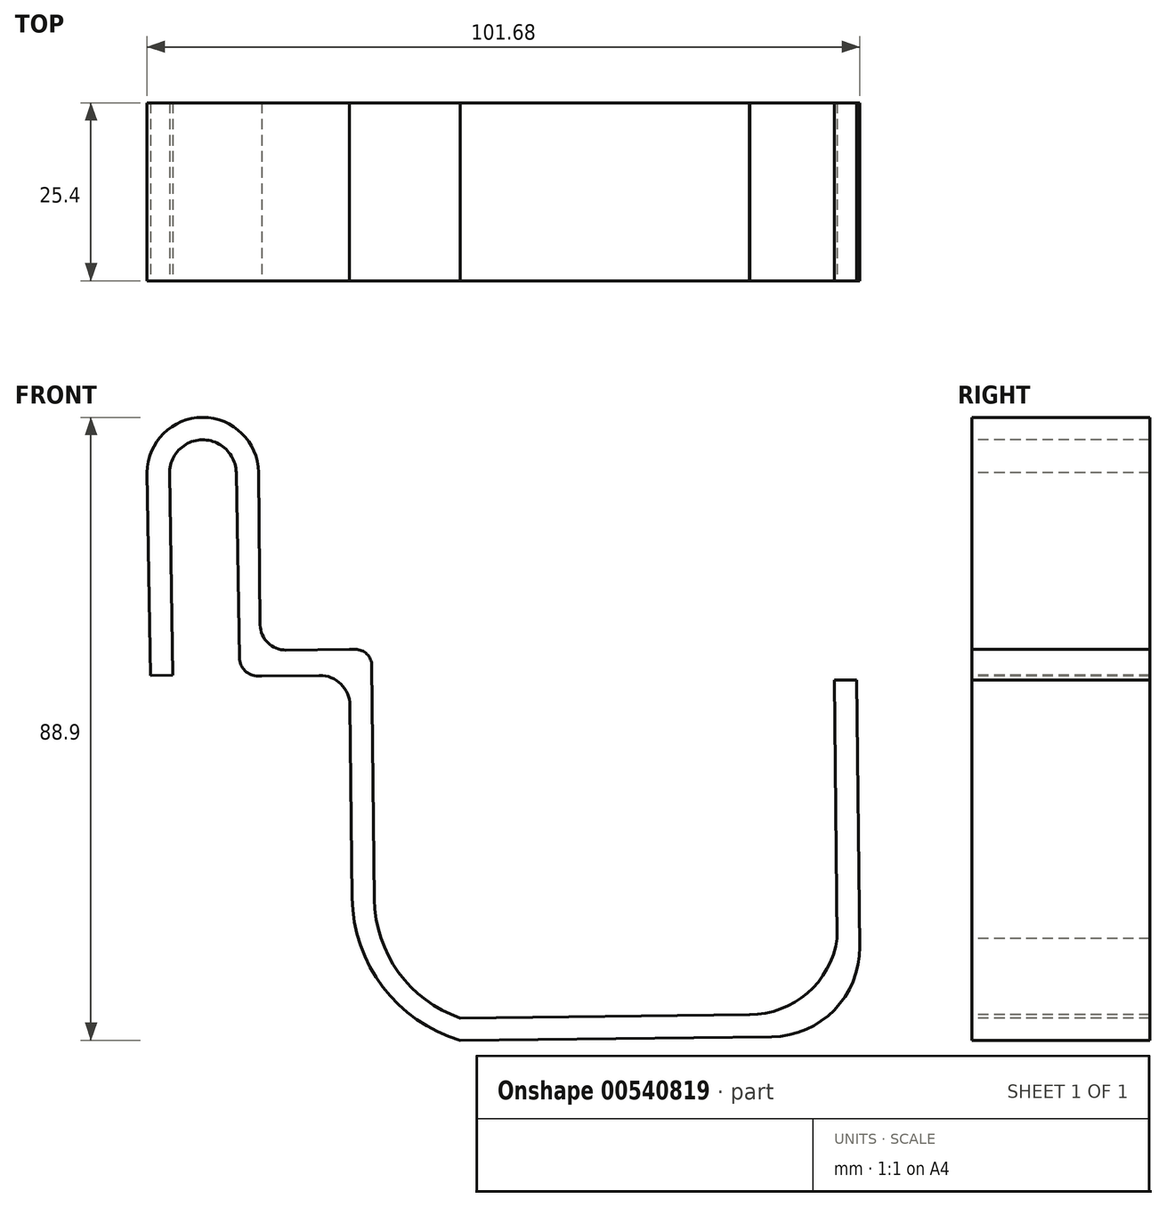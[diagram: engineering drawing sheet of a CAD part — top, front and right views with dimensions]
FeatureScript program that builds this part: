
annotation { "Feature Type Name" : "Feature", "Feature Type Description" : "" }
export const myFeature = defineFeature(function(context is Context, id is Id, definition is map)
    precondition{}
    {
        {
            var Q0;
            Q0=qCreatedBy(makeId("Front.planeOp"),FACE);
            var sketch = newSketch(context, id + "F0", { "sketchPlane" : qUnion([Q0])});
            skLineSegment(sketch, "E0", {"start": v(-53.92, 53.44) * mm, "end": v(-53.55, 20.1) * mm});
            skArc(sketch, "E1", {"start": v(-53.55, 20.1) * mm, "mid": v(-50.12, 9.7) * mm, "end": v(-41.31, 3.17) * mm});
            skLineSegment(sketch, "E2", {"start": v(-41.31, 3.17) * mm, "end": v(0, 3.64) * mm});
            skLineSegment(sketch, "E3", {"start": v(-41.31, 0) * mm, "end": v(3.14, 0.5) * mm});
            skLineSegment(sketch, "E4", {"start": v(-57.04, 47.78) * mm, "end": v(-56.73, 20.32) * mm});
            skLineSegment(sketch, "E5", {"start": v(15.7, 13.34) * mm, "end": v(15.27, 51.44) * mm});
            skLineSegment(sketch, "E6", {"start": v(15.27, 51.44) * mm, "end": v(12.1, 51.4) * mm});
            skLineSegment(sketch, "E7", {"start": v(12.1, 51.4) * mm, "end": v(12.5, 14.5) * mm});
            skLineSegment(sketch, "E8", {"start": v(-0.06, 3.64) * mm, "end": v(0, 3.64) * mm});
            skArc(sketch, "E9.filletArc", {"start": v(-0.06, 3.64) * mm, "mid": v(8.24, 6.73) * mm, "end": v(12.5, 14.5) * mm});
            skArc(sketch, "E10.filletArc", {"start": v(3.14, 0.5) * mm, "mid": v(12.07, 4.32) * mm, "end": v(15.7, 13.34) * mm});
            skArc(sketch, "E11", {"start": v(-56.73, 20.32) * mm, "mid": v(-52.38, 7.62) * mm, "end": v(-41.31, 0) * mm});
            skLineSegment(sketch, "E12", {"start": v(-57.13, 55.79) * mm, "end": v(-66.17, 55.69) * mm});
            skLineSegment(sketch, "E13", {"start": v(-57.13, 55.79) * mm, "end": v(-56.3, 55.79) * mm});
            skLineSegment(sketch, "E14", {"start": v(-61.42, 52.07) * mm, "end": v(-69.6, 51.98) * mm});
            skLineSegment(sketch, "E15", {"start": v(-69.87, 59.3) * mm, "end": v(-70.1, 81.05) * mm});
            skLineSegment(sketch, "E16", {"start": v(-69.6, 51.98) * mm, "end": v(-70.15, 51.98) * mm});
            skLineSegment(sketch, "E17", {"start": v(-72.83, 54.6) * mm, "end": v(-73.28, 81.01) * mm});
            skLineSegment(sketch, "E18", {"start": v(-82.8, 80.84) * mm, "end": v(-82.3, 52.12) * mm});
            skLineSegment(sketch, "E19", {"start": v(-82.3, 52.12) * mm, "end": v(-85.48, 52.07) * mm});
            skLineSegment(sketch, "E20", {"start": v(-85.48, 52.07) * mm, "end": v(-85.99, 81.01) * mm});
            skArc(sketch, "E21", {"start": v(-70.1, 81.05) * mm, "mid": v(-78.06, 88.9) * mm, "end": v(-85.99, 81.01) * mm});
            skArc(sketch, "E22", {"start": v(-73.28, 81.01) * mm, "mid": v(-78.13, 85.69) * mm, "end": v(-82.8, 80.84) * mm});
            skArc(sketch, "E23.filletArc", {"start": v(-57.04, 47.78) * mm, "mid": v(-58.34, 50.83) * mm, "end": v(-61.42, 52.07) * mm});
            skArc(sketch, "E24.filletArc", {"start": v(-53.92, 53.44) * mm, "mid": v(-54.63, 55.1) * mm, "end": v(-56.3, 55.79) * mm});
            skArc(sketch, "E25.filletArc", {"start": v(-69.87, 59.3) * mm, "mid": v(-68.77, 56.73) * mm, "end": v(-66.17, 55.69) * mm});
            skArc(sketch, "E26.filletArc", {"start": v(-72.83, 54.6) * mm, "mid": v(-72.03, 52.75) * mm, "end": v(-70.15, 51.98) * mm});
            skSolve(sketch);
        }
        {
            var Q0;
            Q0=sQuery(id+"F0.wireOp",EDGE,"E18");
            var Q1;
            Q1=sQuery(id+"F0.wireOp",EDGE,"E25.filletArc");
            var Q2;
            Q2=sQuery(id+"F0.wireOp",EDGE,"E2");
            var Q3;
            Q3=sQuery(id+"F0.wireOp",EDGE,"E3");
            var Q4;
            Q4=sQuery(id+"F0.wireOp",EDGE,"E14");
            var Q5;
            Q5=sQuery(id+"F0.wireOp",EDGE,"E19");
            var Q6;
            Q6=sQuery(id+"F0.wireOp",EDGE,"E21");
            var Q7;
            Q7=sQuery(id+"F0.wireOp",EDGE,"E12");
            var Q8;
            Q8=sQuery(id+"F0.wireOp",EDGE,"E10.filletArc");
            var Q9;
            Q9=sQuery(id+"F0.wireOp",EDGE,"E17");
            var Q10;
            Q10=sQuery(id+"F0.wireOp",EDGE,"E23.filletArc");
            var Q11;
            Q11=sQuery(id+"F0.wireOp",EDGE,"E26.filletArc");
            var Q12;
            Q12=sQuery(id+"F0.wireOp",EDGE,"E5");
            var Q13;
            Q13=sQuery(id+"F0.wireOp",EDGE,"E22");
            var Q14;
            Q14=sQuery(id+"F0.wireOp",EDGE,"E9.filletArc");
            var Q15;
            Q15=sQuery(id+"F0.wireOp",EDGE,"E1");
            var Q16;
            Q16=sQuery(id+"F0.wireOp",EDGE,"E7");
            var Q17;
            Q17=sQuery(id+"F0.wireOp",EDGE,"E20");
            var Q18;
            Q18=sQuery(id+"F0.wireOp",EDGE,"E24.filletArc");
            var Q19;
            Q19=sQuery(id+"F0.wireOp",EDGE,"E11");
            var Q20;
            Q20=sQuery(id+"F0.wireOp",EDGE,"E15");
            var Q21;
            Q21=sQuery(id+"F0.wireOp",EDGE,"E0");
            var Q22;
            Q22=sQuery(id+"F0.wireOp",EDGE,"E4");
            var Q23;
            Q23=sQuery(id+"F0.wireOp",EDGE,"E6");
            var Q24;
            Q24=sQuery(id+"F0.wireOp",EDGE,"E16");
            var Q25;
            Q25=sQuery(id+"F0.wireOp",EDGE,"E13");
            var Q26;
            Q26=sQuery(id+"F0.wireOp",EDGE,"E8");
            extrude(context, id + "F1", {"bodyType" : ToolBodyType.SURFACE, "surfaceEntities" : qUnion([Q0, Q1, Q2, Q3, Q4, Q5, Q6, Q7, Q8, Q9, Q10, Q11, Q12, Q13, Q14, Q15, Q16, Q17, Q18, Q19, Q20, Q21, Q22, Q23, Q24, Q25, Q26]), "depth" : 25.4 * mm, "offsetDistance" : 25.4 * mm});
        }
    });
